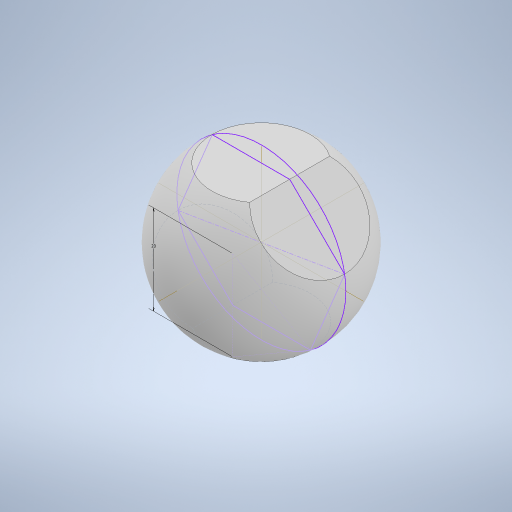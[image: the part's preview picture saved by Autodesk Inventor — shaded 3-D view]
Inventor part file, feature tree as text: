
AUTODESK INVENTOR PART (.ipt)
format: ipt  version: 2023 (Build 270158030, 158C)  size: 313,856 bytes
history: native  units: mm
features: pattern_circular x4, sketch x2, revolve x2, extrude x2, other x1
ambient origin geometry x8: Origin, YZ Plane, XZ Plane, XY Plane, X Axis, Y Axis, Z Axis, Center Point
bodies: Solid5 (feature_tree)
feature tree (11):
  sketch  "Sketch12"  dims[d38=50.0mm d39=0.0mm d43=50.0mm d44=360.0deg d46=50.0mm d47=360.0deg d49=20.0mm d50=90.0deg d51=0.0mm d52=0.0mm d53=50.0mm d54=360.0deg d56=50.0mm d57=360.0deg]
  revolve  "Revolution2"  Angle=90.0deg
  extrude  "Extrusion6"  Depth=50.0mm TaperAngle=360.0deg
  pattern_circular  "Circular Pattern11"  Count=5 Angle=360.0deg
  pattern_circular  "Circular Pattern10"  Count=2  [1 undecoded]
  sketch  "Sketch11"  dims[d36=20.0mm d37=90.0deg]
  revolve  "Revolution1"  Angle=90.0deg
  extrude  "Extrusion5"  TaperAngle=0.0deg  [1 undecoded]
  other  "Work Axis8"
  pattern_circular  "Circular Pattern9"  Count=5 Angle=360.0deg
  pattern_circular  "Circular Pattern8"  Count=5 Angle=360.0deg
note: 2 required parameter values undecoded (feature->parameter linkage not recoverable at this tier; creation-order binding heuristic only, values carry confidence <= 0.55)
